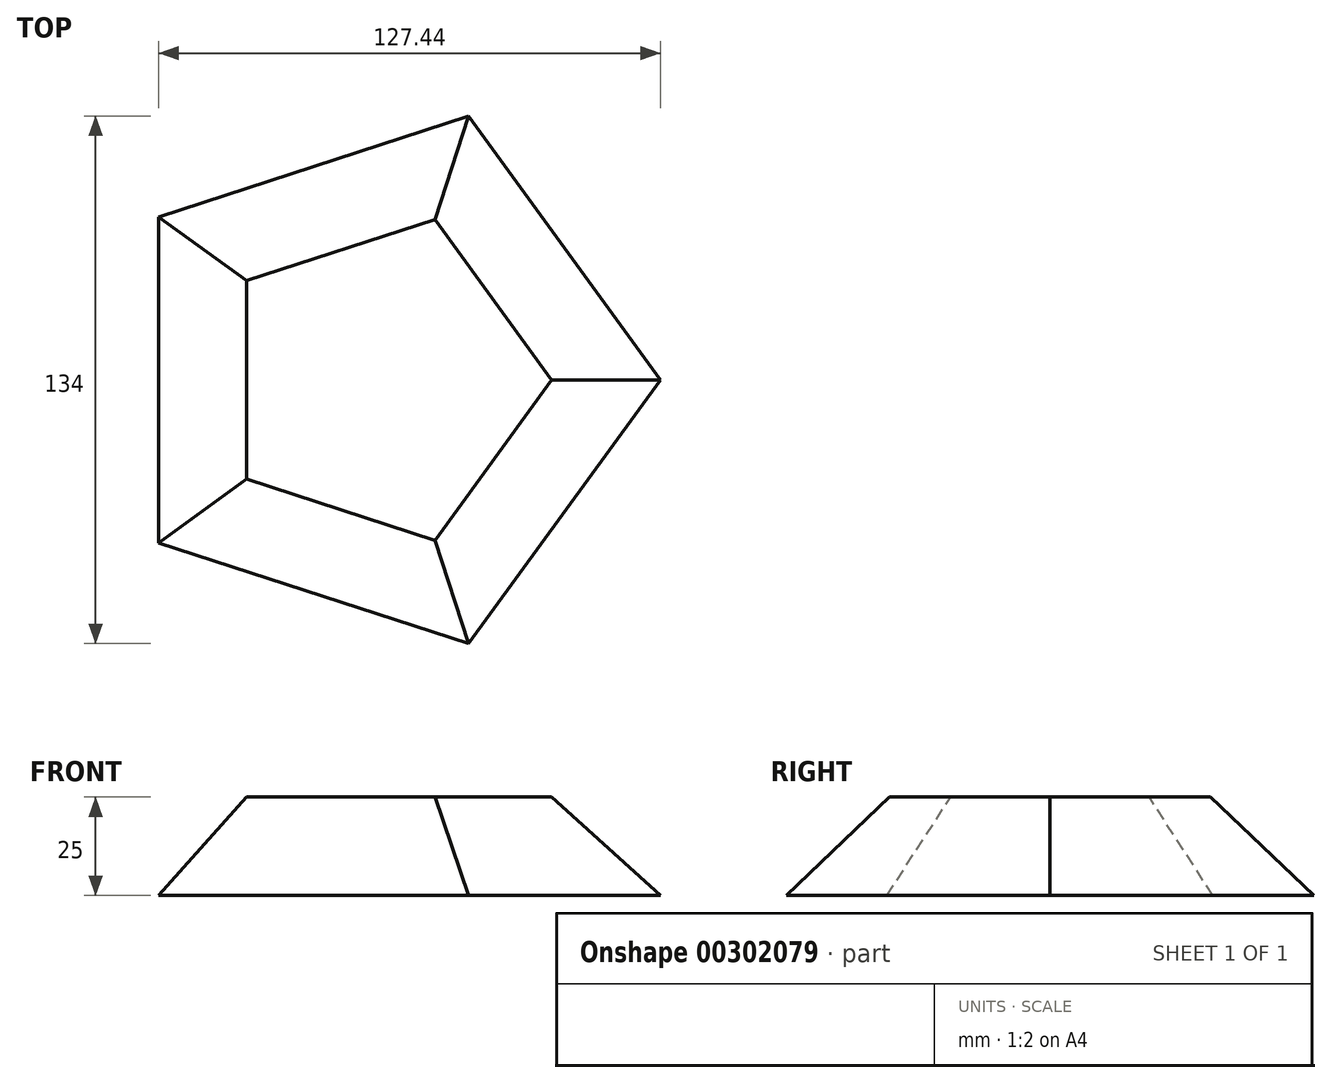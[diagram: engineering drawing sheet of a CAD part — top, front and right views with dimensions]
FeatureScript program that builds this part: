
annotation { "Feature Type Name" : "Feature", "Feature Type Description" : "" }
export const myFeature = defineFeature(function(context is Context, id is Id, definition is map)
    precondition{}
    {
        {
            var Q0;
            Q0=qCreatedBy(makeId("Top.planeOp"),FACE);
            cPlane(context, id + "F0", {"entities" : qUnion([Q0]), "cplaneType" : CPlaneType.OFFSET, "offset" : 25 * mm, "width" : 150 * mm, "height" : 150 * mm});
        }
        {
            var Q0;
            Q0=qCreatedBy(makeId("Top.planeOp"),FACE);
            var sketch = newSketch(context, id + "F1", { "sketchPlane" : qUnion([Q0])});
            skCircle(sketch, "E0.cCircle", {"center": v(0, 0) * mm, "radius": 57 * mm, "construction": true});
            skLineSegment(sketch, "E0.0", {"start": v(-57, -41.4) * mm, "end": v(-57, 41.4) * mm});
            skLineSegment(sketch, "E0.1", {"start": v(-57, 41.4) * mm, "end": v(21.77, 67) * mm});
            skLineSegment(sketch, "E0.2", {"start": v(21.77, 67) * mm, "end": v(70.45, 0) * mm});
            skLineSegment(sketch, "E0.3", {"start": v(70.45, 0) * mm, "end": v(21.77, -67) * mm});
            skLineSegment(sketch, "E0.4", {"start": v(21.77, -67) * mm, "end": v(-57, -41.4) * mm});
            skPoint(sketch, "E0.0.midPoint", {"position": v(-57, 0) * mm});
            skSolve(sketch);
        }
        {
            var Q0;
            Q0=qCreatedBy(id+"F0.planeOp",FACE);
            var sketch = newSketch(context, id + "F2", { "sketchPlane" : qUnion([Q0])});
            skCircle(sketch, "E1.cCircle", {"center": v(0, 0) * mm, "radius": 34.68 * mm, "construction": true});
            skLineSegment(sketch, "E1.0", {"start": v(-34.68, -25.2) * mm, "end": v(-34.68, 25.2) * mm});
            skLineSegment(sketch, "E1.1", {"start": v(-34.68, 25.2) * mm, "end": v(13.25, 40.77) * mm});
            skLineSegment(sketch, "E1.2", {"start": v(13.25, 40.77) * mm, "end": v(42.87, 0) * mm});
            skLineSegment(sketch, "E1.3", {"start": v(42.87, 0) * mm, "end": v(13.25, -40.77) * mm});
            skLineSegment(sketch, "E1.4", {"start": v(13.25, -40.77) * mm, "end": v(-34.68, -25.2) * mm});
            skPoint(sketch, "E1.0.midPoint", {"position": v(-34.68, 0) * mm});
            skSolve(sketch);
        }
        {
            var Q0;
            Q0 = qSketchRegion(id + "F1", true);
            var Q1;
            Q1 = qSketchRegion(id + "F2", true);
            loft(context, id + "F3", {"sheetProfilesArray" : [{ "sheetProfileEntities" : qUnion([Q0]) }, { "sheetProfileEntities" : qUnion([Q1]) }]});
        }
    });
